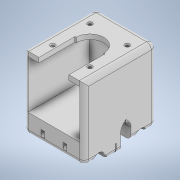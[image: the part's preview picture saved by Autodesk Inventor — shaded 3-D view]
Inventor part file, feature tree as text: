
AUTODESK INVENTOR PART (.ipt)
format: ipt  version: 2022.3 (Build 263350000, 350)  size: 692,736 bytes
history: native  units: mm
features: extrude x12, sketch x10, thicken_offset x10, fillet x4, hole x1, projected_geometry x1
ambient origin geometry x8: Origin, YZ Plane, XZ Plane, XY Plane, X Axis, Y Axis, Z Axis, Center Point
bodies: Solid1 (feature_tree)
feature tree (38):
  extrude  "Extrusion1"  Depth=60.0mm
  extrude  "Extrusion2"  Depth=4.0mm
  sketch  "Sketch3"  dims[d5=25.0mm d6=8.0mm]
  extrude  "Extrusion3"  Depth=8.0mm
  extrude  "Extrusion4"  Depth=43.0mm
  fillet  "Fillet1"  Radius=51.0mm
  extrude  "Extrusion5"  Depth=35.0mm
  hole  "Hole1"  [1 undecoded]
  extrude  "Extrusion6"  Depth=13.0mm TaperAngle=0.0deg
  thicken_offset  "Thicken1"
  thicken_offset  "Thicken2"
  thicken_offset  "Thicken3"
  thicken_offset  "Thicken4"
  thicken_offset  "Thicken5"
  thicken_offset  "Thicken6"
  extrude  "Extrusion7"  Depth=4.0mm
  fillet  "Fillet2"  Radius=22.0mm
  extrude  "Extrusion8"  Depth=42.0mm
  sketch  "Sketch9"  dims[d22=0.0mm d23=0.0mm d24=42.0mm]
  extrude  "Extrusion9"  Depth=4.0mm
  fillet  "Fillet3"  Radius=31.0mm
  extrude  "Extrusion11"  Depth=4.0mm
  extrude  "Extrusion12"  Depth=4.0mm
  thicken_offset  "Thicken8"
  thicken_offset  "Thicken9"
  thicken_offset  "Thicken10"
  thicken_offset  "Thicken11"
  extrude  "Extrusion13"  Depth=4.0mm TaperAngle=0.0deg
  fillet  "Fillet5"  Radius=1.0mm
  sketch  "Sketch1"  dims[d0=50.0mm d1=60.0mm]
  sketch  "Sketch2"  dims[d2=60.5mm d3=0.0mm d4=4.0mm]
  sketch  "Sketch4"  dims[d7=45.0mm d8=43.0mm d9=51.0mm d10=0.0mm]
  sketch  "Sketch5"  dims[d11=17.5mm d12=35.0mm]
  sketch  "Sketch6"  dims[d13=15.0mm d14=15.0mm]
  sketch  "Sketch7"  dims[d15=37.0mm d16=0.0mm d17=13.0mm d18=0.0mm]
  sketch  "Sketch8"  dims[d19=4.0mm d20=18.0mm d21=22.0mm]
  sketch  "Sketch10"  dims[d25=90.0deg d26=31.0mm d27=31.0mm d28=2.4mm d29=6.0mm d30=4.0mm d31=2.0mm d32=90.0deg d33=4.0mm d34=0.0mm d35=9.0mm d36=9.0mm d37=37.0mm d38=0.0mm d39=1.0mm d40=1.0mm d41=1.0mm d42=1.0mm d43=1.0mm d44=1.0mm d45=1.0mm d46=1.0mm d47=5.0mm d48=5.0mm d49=2.0mm d50=2.0mm d51=5.3mm d52=5.3mm d53=3.0mm d54=3.0mm d55=2.0mm d56=2.0mm d57=0.0mm d58=0.0mm d59=3.0mm d60=23.0mm d61=60.5mm d62=0.0mm d63=5.0mm d64=5.0mm d65=4.5mm d66=50.0mm d67=3.0mm d68=1.0mm d69=0.75mm d70=7.0mm d71=0.75mm d72=1.0mm d73=1.0mm d74=1.0mm d75=0.75mm d76=1.0mm d77=0.75mm d78=1.0mm d79=1.0mm d80=0.75mm d81=0.75mm d82=1.0mm d83=0.75mm d84=110.0mm d86=2.0mm d87=10.0mm d89=10.0mm d91=10.0mm d93=10.0mm d94=110.0mm d96=2.0mm d98=10.0mm d99=0.0mm d100=4.0mm d106=3.0mm d107=3.0mm d108=3.5mm d109=0.0mm d110=3.5mm d111=0.0mm d112=4.0mm d113=2.0mm d114=4.0mm d115=2.0mm d116=4.0mm d117=2.0mm d118=4.0mm d119=2.0mm d120=0.0mm d121=0.0mm d122=4.0mm d123=0.0mm d124=0.0mm d125=0.0mm]
  projected_geometry  "Projected Loop1"
note: 1 required parameter value undecoded (feature->parameter linkage not recoverable at this tier; creation-order binding heuristic only, values carry confidence <= 0.55)
